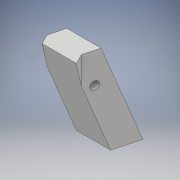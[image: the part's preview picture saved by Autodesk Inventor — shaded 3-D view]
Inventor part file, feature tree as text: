
AUTODESK INVENTOR PART (.ipt)
format: ipt  version: 2017 (Build 210142000, 142)  size: 120,320 bytes
history: native  units: mm
features: plane x6, extrude x2, split x2, sketch x2
ambient origin geometry x8: Origin, YZ Plane, XZ Plane, XY Plane, X Axis, Y Axis, Z Axis, Center Point
bodies: Solid1 (feature_tree)
feature tree (12):
  extrude  "Extrusion1"  Depth=24.14663mm
  plane  "Work Plane1"
  extrude  "Extrusion3"  Depth=22.126mm
  plane  "Work Plane4"
  plane  "Work Plane7"
  split  "Split5"
  split  "Split6"
  sketch  "Sketch1"  dims[d0=24.14663mm d1=24.14663mm]
  sketch  "Sketch3"  dims[d2=15.316mm d3=22.126mm d4=15.0mm d5=2.563889mm d6=40.0mm d7=0.0mm d11=3.5mm d12=26.666667mm d13=13.333333mm d14=15.0mm d15=2.0mm d16=0.0mm d18=11.5mm d19=3.490659mm d20=-4.25mm d21=-6.25mm]
  plane  "Work Plane3"
  plane  "Work Plane5"
  plane  "Work Plane6"
